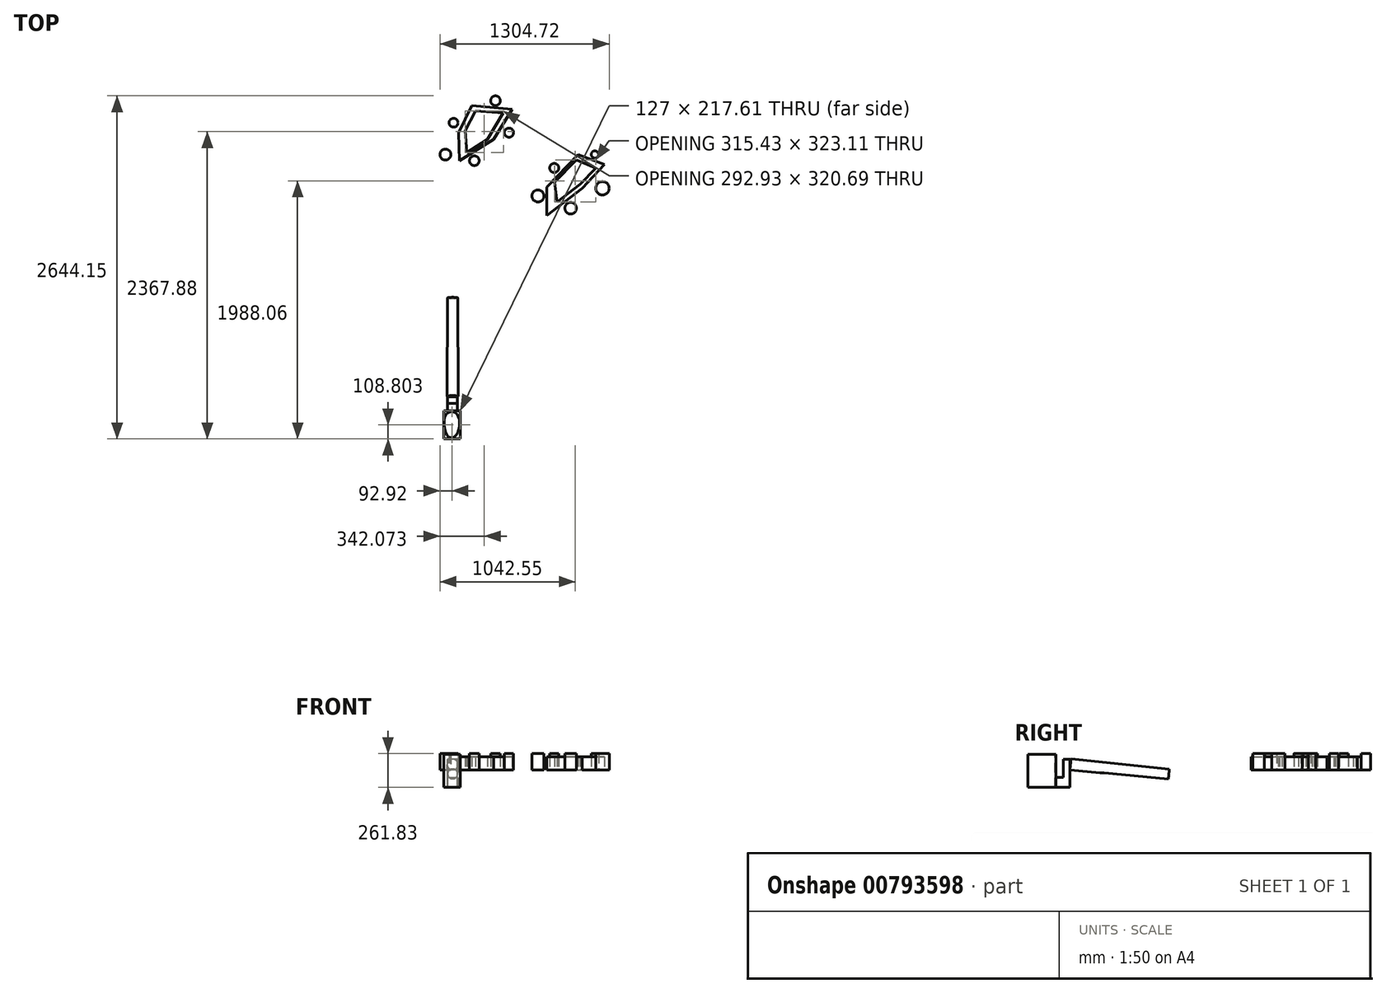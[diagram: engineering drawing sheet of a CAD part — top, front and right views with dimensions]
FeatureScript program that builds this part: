
annotation { "Feature Type Name" : "Feature", "Feature Type Description" : "" }
export const myFeature = defineFeature(function(context is Context, id is Id, definition is map)
    precondition{}
    {
        {
            var Q0;
            Q0=qCreatedBy(makeId("Right.planeOp"),FACE);
            var sketch = newSketch(context, id + "F0", { "sketchPlane" : qUnion([Q0])});
            skLineSegment(sketch, "E0.bottom", {"start": v(-97.08, 119.17) * mm, "end": v(120.53, 119.17) * mm});
            skLineSegment(sketch, "E0.top", {"start": v(-97.08, -134.83) * mm, "end": v(120.53, -134.83) * mm});
            skLineSegment(sketch, "E0.left", {"start": v(-97.08, 119.17) * mm, "end": v(-97.08, -134.83) * mm});
            skLineSegment(sketch, "E0.right", {"start": v(120.53, 119.17) * mm, "end": v(120.53, -134.83) * mm});
            skSolve(sketch);
        }
        {
            var Q0;
            Q0 = qSketchRegion(id + "F0", true);
            extrude(context, id + "F1", {"entities" : qUnion([Q0]), "depth" : 127 * mm, "offsetDistance" : 25.4 * mm});
        }
        {
            var Q0;
            Q0=qCreatedBy(makeId("Front.planeOp"),FACE);
            var sketch = newSketch(context, id + "F2", { "sketchPlane" : qUnion([Q0])});
            skLineSegment(sketch, "E1.bottom", {"start": v(104.02, -58) * mm, "end": v(27.82, -58) * mm});
            skLineSegment(sketch, "E1.top", {"start": v(104.02, -134.2) * mm, "end": v(27.82, -134.2) * mm});
            skLineSegment(sketch, "E1.left", {"start": v(104.02, -134.2) * mm, "end": v(104.02, -58) * mm});
            skLineSegment(sketch, "E1.right", {"start": v(27.82, -134.2) * mm, "end": v(27.82, -58) * mm});
            skSolve(sketch);
        }
        {
            var Q0;
            Q0 = qSketchRegion(id + "F2", true);
            extrude(context, id + "F3", {"entities" : qUnion([Q0]), "operationType" : NewBodyOperationType.ADD, "oppositeDirection" : true, "depth" : 177.8 * mm, "offsetDistance" : 25.4 * mm});
        }
        {
            var Q0;
            Q0=makeQuery(id+"F3.opExtrude","CAP_FACE",FACE,{"disambiguationData":[OSD([sQuery(id+"F2.wireOp",EDGE,"E1.bottom"),sQuery(id+"F2.wireOp",EDGE,"E1.top"),sQuery(id+"F2.wireOp",EDGE,"E1.left"),sQuery(id+"F2.wireOp",EDGE,"E1.right")])],"isStart":false});
            var sketch = newSketch(context, id + "F4", { "sketchPlane" : qUnion([Q0])});
            skLineSegment(sketch, "E2.bottom", {"start": v(-104.02, -134.2) * mm, "end": v(-27.82, -134.2) * mm});
            skLineSegment(sketch, "E2.top", {"start": v(-104.02, 81.24) * mm, "end": v(-27.82, 81.24) * mm});
            skLineSegment(sketch, "E2.left", {"start": v(-104.02, -134.2) * mm, "end": v(-104.02, 81.24) * mm});
            skLineSegment(sketch, "E2.right", {"start": v(-27.82, -134.2) * mm, "end": v(-27.82, 81.24) * mm});
            skSolve(sketch);
        }
        {
            var Q0;
            Q0 = qSketchRegion(id + "F4", true);
            extrude(context, id + "F5", {"entities" : qUnion([Q0]), "operationType" : NewBodyOperationType.ADD, "depth" : 50.8 * mm, "offsetDistance" : 25.4 * mm});
        }
        {
            var Q0;
            Q0=makeQuery(id+"F1.opExtrude","CAP_FACE",FACE,{"disambiguationData":[OSD([sQuery(id+"F0.wireOp",EDGE,"E0.bottom"),sQuery(id+"F0.wireOp",EDGE,"E0.top"),sQuery(id+"F0.wireOp",EDGE,"E0.left"),sQuery(id+"F0.wireOp",EDGE,"E0.right")])],"isStart":false});
            cPlane(context, id + "F6", {"entities" : qUnion([Q0]), "cplaneType" : CPlaneType.OFFSET, "offset" : 58.42 * mm, "oppositeDirection" : true, "width" : 152.4 * mm, "height" : 152.4 * mm});
        }
        {
            var Q0;
            Q0=qCreatedBy(id+"F6.planeOp",FACE);
            var sketch = newSketch(context, id + "F7", { "sketchPlane" : qUnion([Q0])});
            skLineSegment(sketch, "E3.bottom", {"start": v(231.86, 42.07) * mm, "end": v(990.42, -30.3) * mm});
            skLineSegment(sketch, "E3.top", {"start": v(228.07, 0) * mm, "end": v(987, -68.4) * mm});
            skLineSegment(sketch, "E3.left", {"start": v(231.86, 42.07) * mm, "end": v(228.07, 0) * mm});
            skLineSegment(sketch, "E3.right", {"start": v(990.42, -30.3) * mm, "end": v(987, -68.4) * mm});
            skSolve(sketch);
        }
        {
            var Q0;
            Q0 = qSketchRegion(id + "F7", true);
            var Q1;
            Q1=sQuery(id+"F7.wireOp",EDGE,"E3.bottom");
            revolve(context, id + "F8", {"operationType" : NewBodyOperationType.ADD, "surfaceOperationType" : NewSurfaceOperationType.NEW, "entities" : qUnion([Q0]), "axis" : qUnion([Q1]), "revolveType" : RevolveType.FULL});
        }
        {
            var Q0;
            Q0=makeQuery(id+"F1.opExtrude","SWEPT_FACE",FACE,{"disambiguationData":[OSD([sQuery(id+"F0.wireOp",EDGE,"E0.bottom")])]});
            var sketch = newSketch(context, id + "F9", { "sketchPlane" : qUnion([Q0])});
            skFitSpline(sketch, "E4", {"points": [v(96.03, -68.95) * mm, v(104.16, 88.53) * mm, v(21.95, 95.86) * mm, v(29.27, -73.78) * mm, v(96.03, -68.95) * mm]});
            skSolve(sketch);
        }
        {
            var Q0;
            Q0=makeQuery(id+"F9.imprint","IMPRINT",FACE,{"disambiguationData":[TD([[makeQuery(id+"F9.imprint","IMPRINT",EDGE,{"derivedFrom":sQuery(id+"F9.wireOp",EDGE,"E4")}),1.0]])]});
            var Q1;
            Q1=makeQuery(id+"F1.opExtrude","SWEPT_FACE",FACE,{"disambiguationData":[OSD([sQuery(id+"F0.wireOp",EDGE,"E0.top")])]});
            extrude(context, id + "F10", {"entities" : qUnion([Q0]), "operationType" : NewBodyOperationType.REMOVE, "endBound" : BoundingType.UP_TO_SURFACE, "oppositeDirection" : true, "depth" : 25.4 * mm, "endBoundEntityFace" : qUnion([Q1]), "offsetDistance" : 25.4 * mm});
        }
        {
            var Q0;
            Q0=qCreatedBy(makeId("Top.planeOp"),FACE);
            var sketch = newSketch(context, id + "F11", { "sketchPlane" : qUnion([Q0])});
            skLineSegment(sketch, "E5", {"start": v(793.2, 1624.46) * mm, "end": v(1067.02, 1834.38) * mm});
            skLineSegment(sketch, "E6", {"start": v(793.2, 1624.46) * mm, "end": v(793.2, 1844.34) * mm});
            skLineSegment(sketch, "E7", {"start": v(1067.02, 1834.38) * mm, "end": v(1238.4, 2017.8) * mm});
            skLineSegment(sketch, "E8", {"start": v(1238.4, 2017.8) * mm, "end": v(1035.96, 2094.8) * mm});
            skLineSegment(sketch, "E9", {"start": v(793.2, 1844.34) * mm, "end": v(1035.96, 2094.8) * mm});
            skLineSegment(sketch, "E10", {"start": v(122.23, 2047.34) * mm, "end": v(385.76, 2210.67) * mm});
            skLineSegment(sketch, "E11", {"start": v(385.76, 2210.67) * mm, "end": v(527.9, 2444.82) * mm});
            skLineSegment(sketch, "E12", {"start": v(527.9, 2444.82) * mm, "end": v(217.4, 2471.3) * mm});
            skLineSegment(sketch, "E13", {"start": v(217.4, 2471.3) * mm, "end": v(114.54, 2262.08) * mm});
            skLineSegment(sketch, "E14", {"start": v(114.54, 2262.08) * mm, "end": v(122.23, 2047.34) * mm});
            skCircle(sketch, "E15", {"center": v(978.16, 1680.85) * mm, "radius": 44.5 * mm});
            skCircle(sketch, "E16", {"center": v(1223.33, 1834.38) * mm, "radius": 51.96 * mm});
            skCircle(sketch, "E17", {"center": v(1165.03, 2095.11) * mm, "radius": 27.81 * mm});
            skCircle(sketch, "E18", {"center": v(851.82, 1990.87) * mm, "radius": 35.48 * mm});
            skCircle(sketch, "E19", {"center": v(726.14, 1775.57) * mm, "radius": 46.35 * mm});
            skCircle(sketch, "E20", {"center": v(235.54, 2046.75) * mm, "radius": 37.37 * mm});
            skCircle(sketch, "E21", {"center": v(503, 2263.4) * mm, "radius": 35.24 * mm});
            skCircle(sketch, "E22", {"center": v(399.06, 2509.76) * mm, "radius": 37.31 * mm});
            skCircle(sketch, "E23", {"center": v(75.85, 2339.91) * mm, "radius": 34.19 * mm});
            skCircle(sketch, "E24", {"center": v(12.75, 2094.8) * mm, "radius": 42.17 * mm});
            skLineSegment(sketch, "E25", {"start": v(873.48, 1729.42) * mm, "end": v(1049.78, 1864.58) * mm});
            skPoint(sketch, "E25.startSnap0", {"position": v(930.1, 1729.42) * mm});
            skLineSegment(sketch, "E26", {"start": v(1049.78, 1864.58) * mm, "end": v(1170.84, 1989.79) * mm});
            skLineSegment(sketch, "E27", {"start": v(1170.84, 1989.79) * mm, "end": v(1022.1, 2052.54) * mm});
            skLineSegment(sketch, "E28", {"start": v(1022.1, 2052.54) * mm, "end": v(855.42, 1881.29) * mm});
            skLineSegment(sketch, "E29", {"start": v(855.42, 1881.29) * mm, "end": v(873.48, 1729.42) * mm});
            skLineSegment(sketch, "E30", {"start": v(177.13, 2110.46) * mm, "end": v(338.07, 2210.2) * mm});
            skLineSegment(sketch, "E31", {"start": v(338.07, 2210.2) * mm, "end": v(459.12, 2413.5) * mm});
            skLineSegment(sketch, "E32", {"start": v(459.12, 2413.5) * mm, "end": v(243.5, 2431.15) * mm});
            skLineSegment(sketch, "E33", {"start": v(243.5, 2431.15) * mm, "end": v(166.2, 2277.36) * mm});
            skLineSegment(sketch, "E34", {"start": v(166.2, 2277.36) * mm, "end": v(177.13, 2110.46) * mm});
            skSolve(sketch);
        }
        {
            var Q0;
            Q0 = qSketchRegion(id + "F11", true);
            extrude(context, id + "F12", {"entities" : qUnion([Q0]), "depth" : 127 * mm, "offsetDistance" : 25.4 * mm});
        }
        {
            var Q0;
            Q0=makeQuery(id+"F12.opExtrude","CAP_FACE",FACE,{"disambiguationData":[OSD([sQuery(id+"F11.wireOp",EDGE,"E5"),sQuery(id+"F11.wireOp",EDGE,"E6"),sQuery(id+"F11.wireOp",EDGE,"E7"),sQuery(id+"F11.wireOp",EDGE,"E8"),sQuery(id+"F11.wireOp",EDGE,"E9")])],"isStart":false});
            var Q1;
            Q1=makeQuery(id+"F12.opExtrude","CAP_FACE",FACE,{"disambiguationData":[OSD([sQuery(id+"F11.wireOp",EDGE,"E10"),sQuery(id+"F11.wireOp",EDGE,"E11"),sQuery(id+"F11.wireOp",EDGE,"E12"),sQuery(id+"F11.wireOp",EDGE,"E13"),sQuery(id+"F11.wireOp",EDGE,"E14")])],"isStart":false});
            extrude(context, id + "F13", {"entities" : qUnion([Q0, Q1]), "operationType" : NewBodyOperationType.REMOVE, "oppositeDirection" : true, "depth" : 25.4 * mm, "offsetDistance" : 25.4 * mm});
        }
    });
